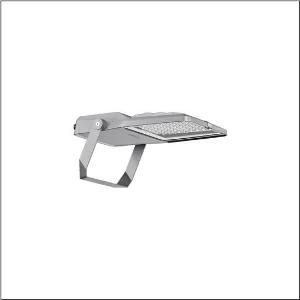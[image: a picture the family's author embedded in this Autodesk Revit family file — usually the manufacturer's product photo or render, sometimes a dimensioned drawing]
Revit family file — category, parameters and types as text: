
# Revit family: floodlight_fl_21_iq_mini___pl61_5xa7771b4c1a_7efd
name_source: partatom
category: Lighting Fixtures
units: mm (PartAtom-declared; Revit-internal decimal feet)

## family parameters
Cut with Voids When Loaded = No
Host = Face
Light Source = No
Part Type = Normal
Room Calculation Point = No
Round Connector Dimension = Use Diameter
Shared = No

## types (1)
- --- (1 x LED, 6370 lm, 45.5 W, 4000K)
    Apparent Load = 46 VA
    CIE Flux Codes = 33 65 98 100 100
    Color Rendering = 70
    Color Temperature = 4000K
    Default Elevation = 1800 mm
    Description = Floodlight FL 21 iQ mini, floodlight, primary light control with lens, of PMMA, primary optical cover: protective disc, of toughened safety glass, transparent, light distribution: PL61, light emission: direct distribution, installation type: surface-mounted, lamps: LED, High Power LED, rated values: 6.370lm | 45,5W | 140lm/W (begin service life); end service life: 6.370lm | 48W; at 50% lumin. flux: 3.185lm | 21,5W | 148,1lm/W, colour temperature: 4000K, colour rendering: CRI > 70, light colour: 740, light setting 1 begin service life: 100% | 6.370lm | 45,5W | 140lm/W | 4.000K, light setting 1 end service life: 48W, further light settings possible, control: Auto-Match, Temp-Guard, Lumen-Switch, Night-Set, Smart-Wire, Light-Fading, Desk-Remote (wireless, voltage-free reading and setting of iQ features in the workshop via application-optimized NFC function/RFID function), optimised constant luminous flux control (CLO 2.0), pre-setting: linear dimming characteristic, with terminal, 6-pole, mains connection: 220..240V, AC, 50/60Hz, luminaire housing, of diecast aluminium, powder-coated, SITECO metallic grey (DB 702S), corrosivity category C5 mid according to DIN EN ISO 12944suitable for swimming poolschlorine-resistant, sealing non-destructively replaceable, mounting bracket, of steel, galvanised, powder-coated, SITECO metallic grey (DB 702S), protection rating (complete): IP66, insulation class (complete): insulation class II (safety insulation), certification: CE, ENEC, VDE, protection symbol: D, impact resistance: IK08, permissible operating ambient temperature: -40..+40°C, permissible operating ambient temperature for outdoor applications: -40..+50°C, standard: DIN EN 12944, LABS conformity tested according to VDMA 24364:2018-05, packaging unit: 1 piece

Light Distribution: PL61
    Height = 70 mm
    Lamp = 1 x LED
    Lamp Light Flux = 6370 lm
    Lamp Power = 45.5 W
    Lamp count = 1
    Length = 485 mm
    Luminous efficacy = 140 lm/W
    Manufacturer = Siteco
    ModVariant = No
    Model = 5XA7771B4C1A
    Mounting Place = Wall
    Mounting Type = Surface mounted
    Number of Poles = 1
    OnlyDefault = Yes
    Power Factor = 1
    Product Name = Floodlight FL 21 iQ mini | PL61
    Product group = floodlight | wall mounted
    ProductGroupID = 2002
    Protection Class = Protection class II
    Protection Degree = IP 66
    RLX_Detail_Level = 1
    RLX_Emergency_Light_Flux = 0 lm
    RLX_Emergency_Type = 0
    RLX_Emergency_Type_DB = No
    RlxData = <blob elided: 96525 chars, md5=7c45e5bf>
    Socket = socket
    Standby Power = 0 W
    System Light Flux = 6370 lm
    System Power = 46 W
    Type Comments = factory setting: luminous flux: 100 % | dim-lin: 254 | 463 mA
    Type Image = l_1006845.jpg
    URL = http://relux.com
    VarID = @adj_174841
    Voltage = 0 V
    Weight = 0.00 kg
    Width = 337 mm

## geometry (parser evidence)
native form markers: Blend x4, Sweep x11
no freeform markers — native parametric forms only
